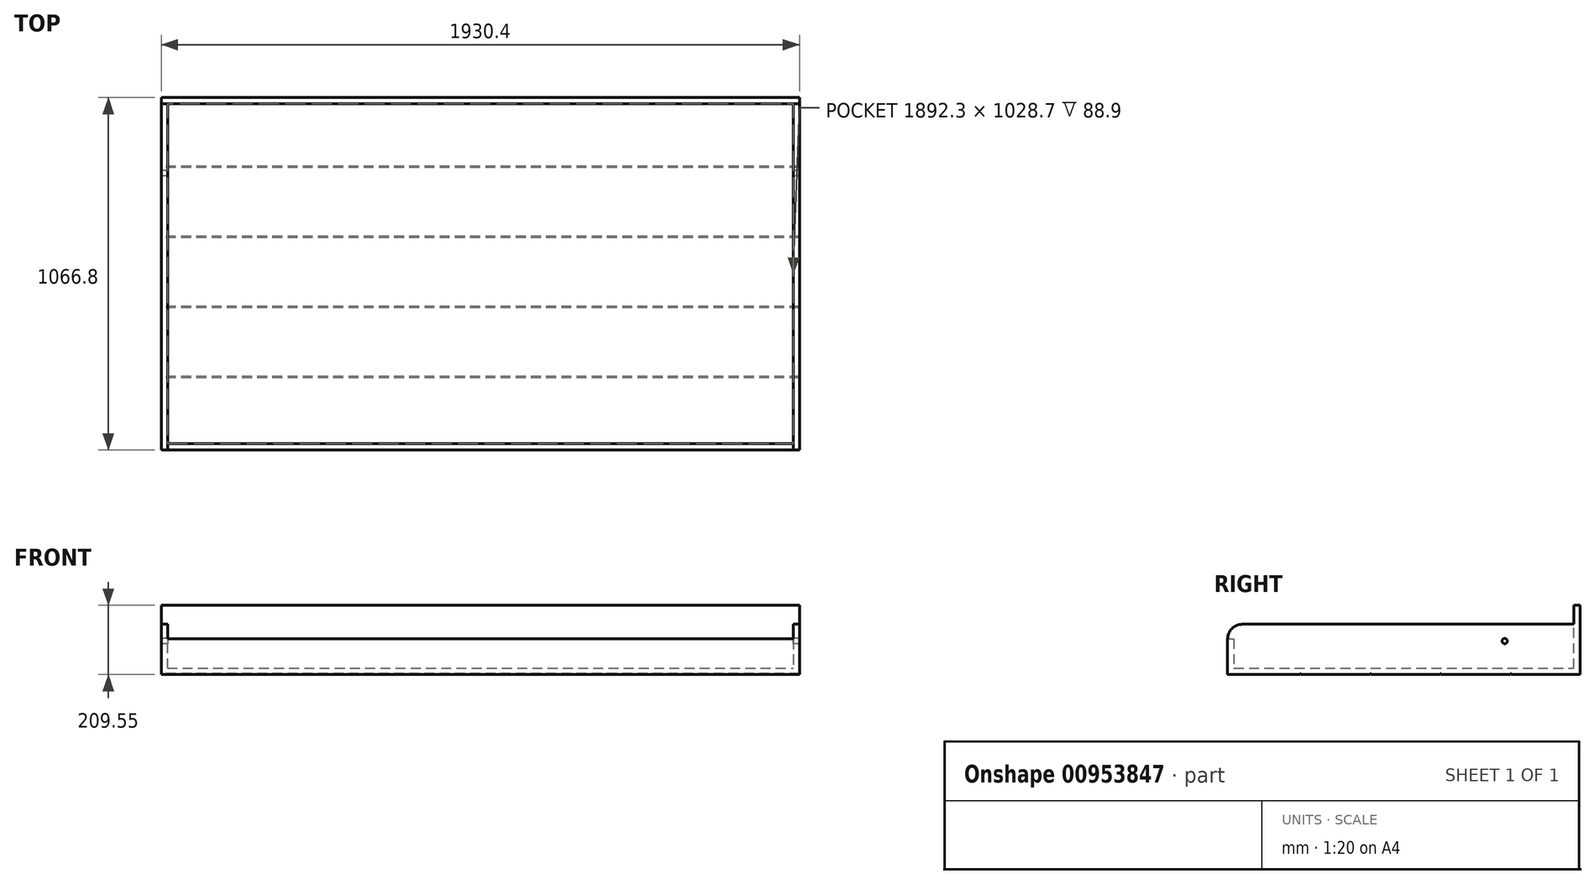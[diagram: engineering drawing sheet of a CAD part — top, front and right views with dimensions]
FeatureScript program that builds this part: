
annotation { "Feature Type Name" : "Feature", "Feature Type Description" : "" }
export const myFeature = defineFeature(function(context is Context, id is Id, definition is map)
    precondition{}
    {
        {
            var Q0;
            Q0=qCreatedBy(makeId("Top.planeOp"),FACE);
            var sketch = newSketch(context, id + "F0", { "sketchPlane" : qUnion([Q0])});
            skLineSegment(sketch, "E0.bottom", {"start": v(-965.2, 533.4) * mm, "end": v(965.2, 533.4) * mm});
            skLineSegment(sketch, "E0.top", {"start": v(-965.2, -533.4) * mm, "end": v(965.2, -533.4) * mm});
            skLineSegment(sketch, "E0.left", {"start": v(-965.2, 533.4) * mm, "end": v(-965.2, -533.4) * mm});
            skLineSegment(sketch, "E0.right", {"start": v(965.2, 533.4) * mm, "end": v(965.2, -533.4) * mm});
            skPoint(sketch, "E0.middle", {"position": v(0, 0) * mm});
            skSolve(sketch);
        }
        {
            var Q0;
            Q0 = qSketchRegion(id + "F0", true);
            extrude(context, id + "F1", {"entities" : qUnion([Q0]), "depth" : 19.05 * mm, "offsetDistance" : 25.4 * mm});
        }
        {
            var Q0;
            Q0=makeQuery(id+"F1.opExtrude","CAP_FACE",FACE,{"disambiguationData":[OSD([sQuery(id+"F0.wireOp",EDGE,"E0.bottom"),sQuery(id+"F0.wireOp",EDGE,"E0.top"),sQuery(id+"F0.wireOp",EDGE,"E0.left"),sQuery(id+"F0.wireOp",EDGE,"E0.right")])],"isStart":false});
            var sketch = newSketch(context, id + "F2", { "sketchPlane" : qUnion([Q0])});
            skLineSegment(sketch, "E1.bottom", {"start": v(-965.2, -533.4) * mm, "end": v(965.2, -533.4) * mm});
            skLineSegment(sketch, "E1.top", {"start": v(-965.2, -514.35) * mm, "end": v(965.2, -514.35) * mm});
            skLineSegment(sketch, "E1.left", {"start": v(-965.2, -533.4) * mm, "end": v(-965.2, -514.35) * mm});
            skLineSegment(sketch, "E1.right", {"start": v(965.2, -533.4) * mm, "end": v(965.2, -514.35) * mm});
            skSolve(sketch);
        }
        {
            var Q0;
            Q0 = qSketchRegion(id + "F2", true);
            extrude(context, id + "F3", {"entities" : qUnion([Q0]), "operationType" : NewBodyOperationType.ADD, "depth" : 88.9 * mm, "offsetDistance" : 25.4 * mm});
        }
        {
            var Q0;
            Q0=makeQuery(id+"F1.opExtrude","CAP_FACE",FACE,{"disambiguationData":[OSD([sQuery(id+"F0.wireOp",EDGE,"E0.bottom"),sQuery(id+"F0.wireOp",EDGE,"E0.top"),sQuery(id+"F0.wireOp",EDGE,"E0.left"),sQuery(id+"F0.wireOp",EDGE,"E0.right")])],"isStart":false});
            var sketch = newSketch(context, id + "F4", { "sketchPlane" : qUnion([Q0])});
            skLineSegment(sketch, "E2.bottom", {"start": v(-965.2, 533.4) * mm, "end": v(965.2, 533.4) * mm});
            skLineSegment(sketch, "E2.top", {"start": v(-965.2, 514.35) * mm, "end": v(965.2, 514.35) * mm});
            skLineSegment(sketch, "E2.left", {"start": v(-965.2, 533.4) * mm, "end": v(-965.2, 514.35) * mm});
            skLineSegment(sketch, "E2.right", {"start": v(965.2, 533.4) * mm, "end": v(965.2, 514.35) * mm});
            skSolve(sketch);
        }
        {
            var Q0;
            Q0 = qSketchRegion(id + "F4", true);
            extrude(context, id + "F5", {"entities" : qUnion([Q0]), "operationType" : NewBodyOperationType.ADD, "depth" : 190.5 * mm, "offsetDistance" : 25.4 * mm});
        }
        {
            var Q0;
            Q0=makeQuery(id+"F5.boolean.opBoolean","MERGE",FACE,{"derivedFrom":[makeQuery(id+"F3.boolean.opBoolean","MERGE",FACE,{"derivedFrom":[makeQuery(id+"F1.opExtrude","SWEPT_FACE",FACE,{"disambiguationData":[OSD([sQuery(id+"F0.wireOp",EDGE,"E0.left")])]}),makeQuery(id+"F3.opExtrude","SWEPT_FACE",FACE,{"disambiguationData":[OSD([sQuery(id+"F2.wireOp",EDGE,"E1.left")])]})]}),makeQuery(id+"F5.opExtrude","SWEPT_FACE",FACE,{"disambiguationData":[OSD([sQuery(id+"F4.wireOp",EDGE,"E2.left")])]})]});
            var sketch = newSketch(context, id + "F6", { "sketchPlane" : qUnion([Q0])});
            skLineSegment(sketch, "E3.bottom", {"start": v(533.4, 0) * mm, "end": v(-533.4, 0) * mm});
            skLineSegment(sketch, "E3.top", {"start": v(488.95, 152.4) * mm, "end": v(-533.4, 152.4) * mm});
            skLineSegment(sketch, "E3.left", {"start": v(533.4, 0) * mm, "end": v(533.4, 107.95) * mm});
            skLineSegment(sketch, "E3.right", {"start": v(-533.4, 0) * mm, "end": v(-533.4, 152.4) * mm});
            skPoint(sketch, "E4.visualSharp", {"position": v(533.4, 152.4) * mm});
            skArc(sketch, "E4.filletArc", {"start": v(533.4, 107.95) * mm, "mid": v(520.38, 139.38) * mm, "end": v(488.95, 152.4) * mm});
            skSolve(sketch);
        }
        {
            var Q0;
            Q0 = qSketchRegion(id + "F6", true);
            extrude(context, id + "F7", {"entities" : qUnion([Q0]), "operationType" : NewBodyOperationType.ADD, "oppositeDirection" : true, "depth" : 19.05 * mm, "offsetDistance" : 25.4 * mm});
        }
        {
            var Q0;
            Q0=makeQuery(id+"F5.boolean.opBoolean","MERGE",FACE,{"derivedFrom":[makeQuery(id+"F3.boolean.opBoolean","MERGE",FACE,{"derivedFrom":[makeQuery(id+"F1.opExtrude","SWEPT_FACE",FACE,{"disambiguationData":[OSD([sQuery(id+"F0.wireOp",EDGE,"E0.right")])]}),makeQuery(id+"F3.opExtrude","SWEPT_FACE",FACE,{"disambiguationData":[OSD([sQuery(id+"F2.wireOp",EDGE,"E1.right")])]})]}),makeQuery(id+"F5.opExtrude","SWEPT_FACE",FACE,{"disambiguationData":[OSD([sQuery(id+"F4.wireOp",EDGE,"E2.right")])]})]});
            var sketch = newSketch(context, id + "F8", { "sketchPlane" : qUnion([Q0])});
            skLineSegment(sketch, "E5", {"start": v(-533.4, 0) * mm, "end": v(533.4, 0) * mm});
            skLineSegment(sketch, "E6", {"start": v(-533.4, 0) * mm, "end": v(-533.4, 107.95) * mm});
            skArc(sketch, "E7", {"start": v(-488.95, 152.4) * mm, "mid": v(-520.38, 139.38) * mm, "end": v(-533.4, 107.95) * mm});
            skLineSegment(sketch, "E8", {"start": v(-488.95, 152.4) * mm, "end": v(533.4, 152.4) * mm});
            skLineSegment(sketch, "E9", {"start": v(533.4, 0) * mm, "end": v(533.4, 152.4) * mm});
            skSolve(sketch);
        }
        {
            var Q0;
            Q0 = qSketchRegion(id + "F8", true);
            extrude(context, id + "F9", {"entities" : qUnion([Q0]), "operationType" : NewBodyOperationType.ADD, "oppositeDirection" : true, "depth" : 19.05 * mm, "offsetDistance" : 25.4 * mm});
        }
        {
            var Q0;
            Q0=makeQuery(id+"F7.boolean.opBoolean","MERGE",FACE,{"derivedFrom":[makeQuery(id+"F5.boolean.opBoolean","MERGE",FACE,{"derivedFrom":[makeQuery(id+"F3.boolean.opBoolean","MERGE",FACE,{"derivedFrom":[makeQuery(id+"F1.opExtrude","SWEPT_FACE",FACE,{"disambiguationData":[OSD([sQuery(id+"F0.wireOp",EDGE,"E0.left")])]}),makeQuery(id+"F3.opExtrude","SWEPT_FACE",FACE,{"disambiguationData":[OSD([sQuery(id+"F2.wireOp",EDGE,"E1.left")])]})]}),makeQuery(id+"F5.opExtrude","SWEPT_FACE",FACE,{"disambiguationData":[OSD([sQuery(id+"F4.wireOp",EDGE,"E2.left")])]})]}),makeQuery(id+"F7.opExtrude","CAP_FACE",FACE,{"disambiguationData":[OSD([sQuery(id+"F6.wireOp",EDGE,"E3.bottom"),sQuery(id+"F6.wireOp",EDGE,"E3.top"),sQuery(id+"F6.wireOp",EDGE,"E3.left"),sQuery(id+"F6.wireOp",EDGE,"E3.right"),sQuery(id+"F6.wireOp",EDGE,"E4.filletArc")])],"isStart":true})]});
            var sketch = newSketch(context, id + "F10", { "sketchPlane" : qUnion([Q0])});
            skCircle(sketch, "E10", {"center": v(-304.8, 101.6) * mm, "radius": 7.94 * mm});
            skSolve(sketch);
        }
        {
            var Q0;
            Q0 = qSketchRegion(id + "F10", true);
            extrude(context, id + "F11", {"entities" : qUnion([Q0]), "operationType" : NewBodyOperationType.REMOVE, "endBound" : BoundingType.THROUGH_ALL, "oppositeDirection" : true, "depth" : 25.4 * mm, "offsetDistance" : 25.4 * mm});
        }
        {
            var Q0;
            Q0=makeQuery(id+"F7.boolean.opBoolean","MERGE",FACE,{"derivedFrom":[makeQuery(id+"F5.boolean.opBoolean","MERGE",FACE,{"derivedFrom":[makeQuery(id+"F3.boolean.opBoolean","MERGE",FACE,{"derivedFrom":[makeQuery(id+"F1.opExtrude","SWEPT_FACE",FACE,{"disambiguationData":[OSD([sQuery(id+"F0.wireOp",EDGE,"E0.left")])]}),makeQuery(id+"F3.opExtrude","SWEPT_FACE",FACE,{"disambiguationData":[OSD([sQuery(id+"F2.wireOp",EDGE,"E1.left")])]})]}),makeQuery(id+"F5.opExtrude","SWEPT_FACE",FACE,{"disambiguationData":[OSD([sQuery(id+"F4.wireOp",EDGE,"E2.left")])]})]}),makeQuery(id+"F7.opExtrude","CAP_FACE",FACE,{"disambiguationData":[OSD([sQuery(id+"F6.wireOp",EDGE,"E3.bottom"),sQuery(id+"F6.wireOp",EDGE,"E3.top"),sQuery(id+"F6.wireOp",EDGE,"E3.left"),sQuery(id+"F6.wireOp",EDGE,"E3.right"),sQuery(id+"F6.wireOp",EDGE,"E4.filletArc")])],"isStart":true})]});
            var sketch = newSketch(context, id + "F12", { "sketchPlane" : qUnion([Q0])});
            skLineSegment(sketch, "E11.bottom", {"start": v(-325.12, 0) * mm, "end": v(-321.94, 0) * mm});
            skLineSegment(sketch, "E11.top", {"start": v(-325.12, 3.18) * mm, "end": v(-321.94, 3.18) * mm});
            skLineSegment(sketch, "E11.left", {"start": v(-325.12, 0) * mm, "end": v(-325.12, 3.18) * mm});
            skLineSegment(sketch, "E11.right", {"start": v(-321.94, 0) * mm, "end": v(-321.94, 3.18) * mm});
            skLineSegment(sketch, "E12.1.0.0", {"start": v(-113.03, 3.18) * mm, "end": v(-109.85, 3.18) * mm});
            skLineSegment(sketch, "E12.1.0.1", {"start": v(-113.03, 0) * mm, "end": v(-113.03, 3.18) * mm});
            skLineSegment(sketch, "E12.1.0.2", {"start": v(-109.85, 0) * mm, "end": v(-109.85, 3.18) * mm});
            skLineSegment(sketch, "E12.1.0.3", {"start": v(-113.03, 0) * mm, "end": v(-109.85, 0) * mm});
            skLineSegment(sketch, "E12.2.0.0", {"start": v(99.06, 3.18) * mm, "end": v(102.24, 3.18) * mm});
            skLineSegment(sketch, "E12.2.0.1", {"start": v(99.06, 0) * mm, "end": v(99.06, 3.18) * mm});
            skLineSegment(sketch, "E12.2.0.2", {"start": v(102.24, 0) * mm, "end": v(102.24, 3.18) * mm});
            skLineSegment(sketch, "E12.2.0.3", {"start": v(99.06, 0) * mm, "end": v(102.24, 0) * mm});
            skLineSegment(sketch, "E12.3.0.0", {"start": v(311.15, 3.18) * mm, "end": v(314.33, 3.18) * mm});
            skLineSegment(sketch, "E12.3.0.1", {"start": v(311.15, 0) * mm, "end": v(311.15, 3.18) * mm});
            skLineSegment(sketch, "E12.3.0.2", {"start": v(314.33, 0) * mm, "end": v(314.33, 3.18) * mm});
            skLineSegment(sketch, "E12.3.0.3", {"start": v(311.15, 0) * mm, "end": v(314.33, 0) * mm});
            skLineSegment(sketch, "E12.direction1", {"start": v(-325.12, 0) * mm, "end": v(-113.03, 0) * mm, "construction": true});
            skSolve(sketch);
        }
        {
            var Q0;
            Q0 = qSketchRegion(id + "F12", true);
            var Q1;
            Q1=makeQuery(id+"F9.boolean.opBoolean","MERGE",FACE,{"derivedFrom":[makeQuery(id+"F5.boolean.opBoolean","MERGE",FACE,{"derivedFrom":[makeQuery(id+"F3.boolean.opBoolean","MERGE",FACE,{"derivedFrom":[makeQuery(id+"F1.opExtrude","SWEPT_FACE",FACE,{"disambiguationData":[OSD([sQuery(id+"F0.wireOp",EDGE,"E0.right")])]}),makeQuery(id+"F3.opExtrude","SWEPT_FACE",FACE,{"disambiguationData":[OSD([sQuery(id+"F2.wireOp",EDGE,"E1.right")])]})]}),makeQuery(id+"F5.opExtrude","SWEPT_FACE",FACE,{"disambiguationData":[OSD([sQuery(id+"F4.wireOp",EDGE,"E2.right")])]})]}),makeQuery(id+"F9.opExtrude","CAP_FACE",FACE,{"disambiguationData":[OSD([sQuery(id+"F8.wireOp",EDGE,"E5"),sQuery(id+"F8.wireOp",EDGE,"E6"),sQuery(id+"F8.wireOp",EDGE,"E7"),sQuery(id+"F8.wireOp",EDGE,"E8"),sQuery(id+"F8.wireOp",EDGE,"E9")])],"isStart":true})]});
            extrude(context, id + "F13", {"entities" : qUnion([Q0]), "operationType" : NewBodyOperationType.REMOVE, "endBound" : BoundingType.UP_TO_SURFACE, "oppositeDirection" : true, "depth" : 25.4 * mm, "endBoundEntityFace" : qUnion([Q1]), "offsetDistance" : 25.4 * mm});
        }
    });
